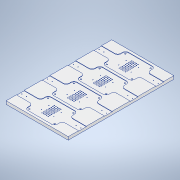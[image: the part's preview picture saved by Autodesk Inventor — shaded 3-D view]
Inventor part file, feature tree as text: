
AUTODESK INVENTOR PART (.ipt)
format: ipt  version: 2022 (Build 260153000, 153)  size: 519,680 bytes
history: native  units: in
note: dims shown in document units (in); Inventor stores cm internally (conversion verified against a paired STEP export)
features: sketch x5, hole x3, extrude x2
ambient origin geometry x8: Origin, YZ Plane, XZ Plane, XY Plane, X Axis, Y Axis, Z Axis, Center Point
bodies: Solid1 (feature_tree)
feature tree (10):
  extrude  "Extrusion1"  Depth=5.0in
  extrude  "Extrusion2"  Depth=2.375in
  hole  "Hole1"  [1 undecoded]
  hole  "Hole2"  [1 undecoded]
  hole  "Hole3"  [1 undecoded]
  sketch  "Sketch1"  dims[d0=8.5in d1=5.0in]
  sketch  "Sketch2"  dims[d2=0.25in d3=0.0in d4=2.375in]
  sketch  "Sketch3"  dims[d5=1.875in d6=0.625in]
  sketch  "Sketch4"  dims[d7=0.25in d8=0.25in]
  sketch  "Sketch5"  dims[d9=0.625in d10=0.625in d11=0.625in d12=1.5748in d14=2.075in d15=0.3937in d17=1.0in d19=0.2in d20=0.034in d21=0.0in d22=0.5in d23=0.3125in d25=0.5in d26=1.5748in d28=2.075in d29=0.3937in d31=1.0in d33=0.0402in d34=0.094in d35=0.217in d36=0.25in d37=90.0deg d38=1.0in d39=0.8108in d40=0.125in d41=0.125in d42=1.5748in d44=2.075in d45=0.3937in d47=1.0in d59=1.5748in d61=2.075in d62=0.3937in d64=1.0in d66=0.0984in d67=0.75in d68=0.217in d69=0.25in d70=90.0deg d71=1.0in d72=0.8108in d73=0.9375in d75=0.5in d76=0.25in d77=3.5433in d79=0.125in d80=1.9685in d82=0.125in d85=1.5748in d87=2.075in d88=0.3937in d90=1.0in d92=0.0625in d93=0.75in d94=0.375in d95=0.25in d96=0.5635in d97=1.0in d98=0.8108in d99=2.0in d100=0.3in d101=0.3in d102=2.0in d103=1.5748in d105=2.075in d106=0.3937in d108=1.0in]
note: 3 required parameter values undecoded (feature->parameter linkage not recoverable at this tier; creation-order binding heuristic only, values carry confidence <= 0.55)
